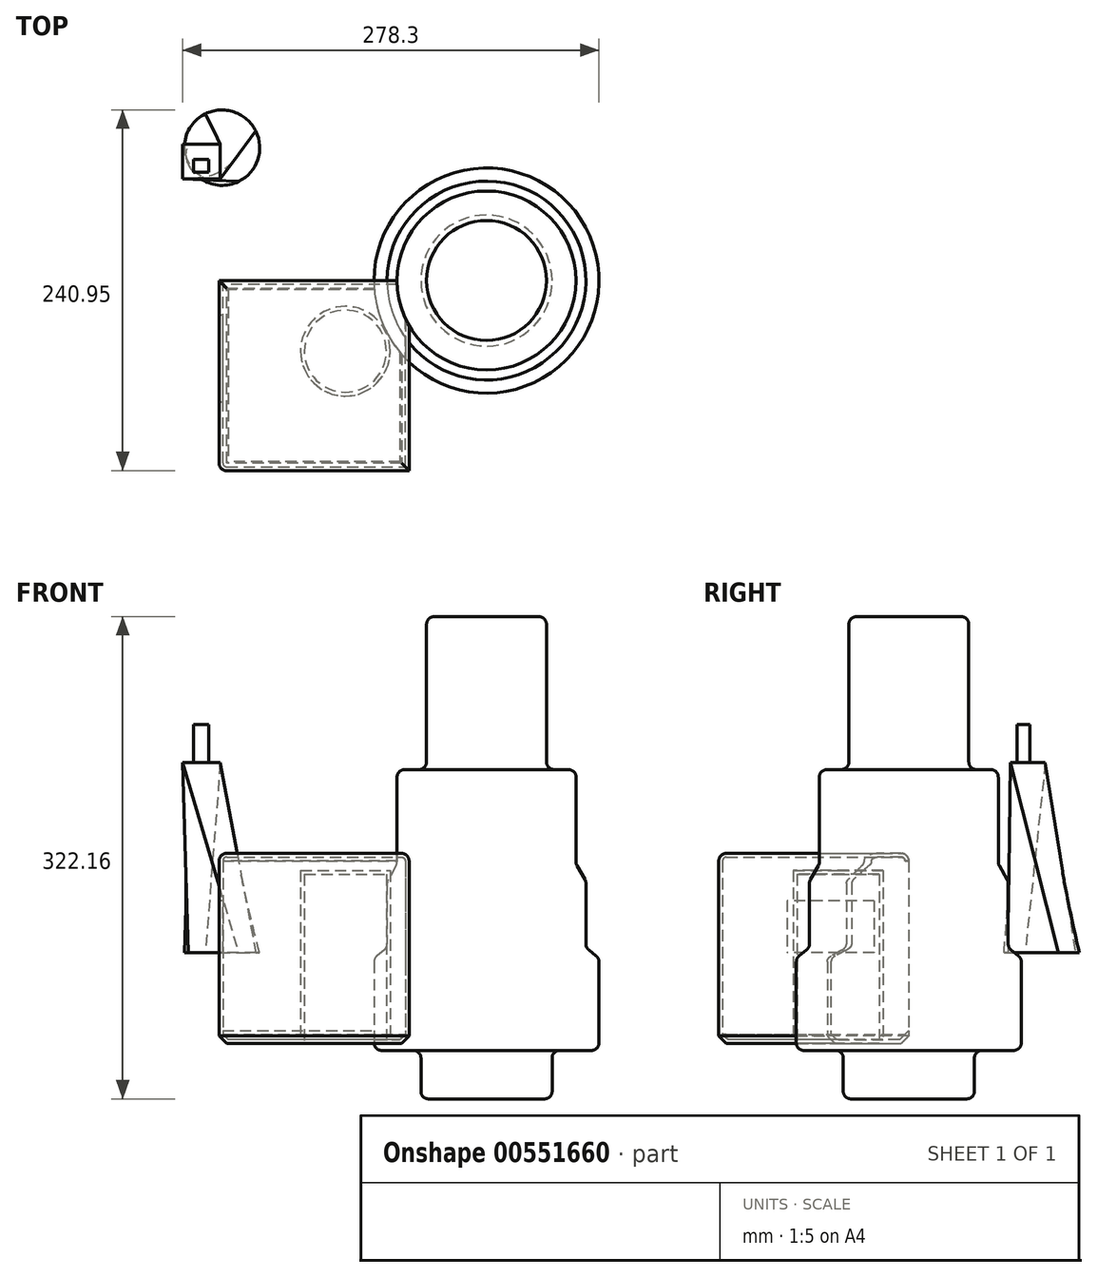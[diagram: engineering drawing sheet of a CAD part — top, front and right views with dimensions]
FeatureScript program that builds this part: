
annotation { "Feature Type Name" : "Feature", "Feature Type Description" : "" }
export const myFeature = defineFeature(function(context is Context, id is Id, definition is map)
    precondition{}
    {
        {
            var Q0;
            Q0=qCreatedBy(makeId("Front.planeOp"),FACE);
            var sketch = newSketch(context, id + "F0", { "sketchPlane" : qUnion([Q0])});
            skLineSegment(sketch, "E0.bottom", {"start": v(-66.33, 66.48) * mm, "end": v(60.67, 66.48) * mm});
            skLineSegment(sketch, "E0.top", {"start": v(-66.33, -60.52) * mm, "end": v(60.67, -60.52) * mm});
            skLineSegment(sketch, "E0.left", {"start": v(-66.33, 66.48) * mm, "end": v(-66.33, -60.52) * mm});
            skLineSegment(sketch, "E0.right", {"start": v(60.67, 66.48) * mm, "end": v(60.67, -60.52) * mm});
            skSolve(sketch);
        }
        {
            var Q0;
            Q0=makeQuery(id+"F0.imprint","IMPRINT",FACE,{"disambiguationData":[TD([[makeQuery(id+"F0.imprint","IMPRINT",EDGE,{"derivedFrom":sQuery(id+"F0.wireOp",EDGE,"E0.bottom")}),-1.0]])]});
            extrude(context, id + "F1", {"entities" : qUnion([Q0]), "depth" : 127 * mm, "offsetDistance" : 25.4 * mm});
        }
        {
            var Q0;
            Q0=makeQuery(id+"F1.opExtrude","SWEPT_FACE",FACE,{"disambiguationData":[OSD([sQuery(id+"F0.wireOp",EDGE,"E0.top")])]});
            var sketch = newSketch(context, id + "F2", { "sketchPlane" : qUnion([Q0])});
            skCircle(sketch, "E1", {"center": v(18.1, 47.2) * mm, "radius": 27.41 * mm});
            skSolve(sketch);
        }
        {
            var Q0;
            Q0=makeQuery(id+"F2.imprint","IMPRINT",FACE,{"disambiguationData":[TD([[makeQuery(id+"F2.imprint","IMPRINT",EDGE,{"derivedFrom":sQuery(id+"F2.wireOp",EDGE,"E1")}),1.0]])]});
            extrude(context, id + "F3", {"entities" : qUnion([Q0]), "operationType" : NewBodyOperationType.REMOVE, "oppositeDirection" : true, "depth" : 113.03 * mm, "offsetDistance" : 25.4 * mm});
        }
        {
            var Q0;
            Q0=qCreatedBy(makeId("Top.planeOp"),FACE);
            var sketch = newSketch(context, id + "F4", { "sketchPlane" : qUnion([Q0])});
            skCircle(sketch, "E2", {"center": v(-64.33, 88.76) * mm, "radius": 25.19 * mm});
            skSolve(sketch);
        }
        {
            var Q0;
            Q0=makeQuery(id+"F4.imprint","IMPRINT",FACE,{"disambiguationData":[TD([[makeQuery(id+"F4.imprint","IMPRINT",EDGE,{"derivedFrom":sQuery(id+"F4.wireOp",EDGE,"E2")}),1.0]])]});
            cPlane(context, id + "F5", {"entities" : qUnion([Q0]), "cplaneType" : CPlaneType.OFFSET, "offset" : 127 * mm, "width" : 152.4 * mm, "height" : 152.4 * mm});
        }
        {
            var Q0;
            Q0=qCreatedBy(id+"F5.planeOp",FACE);
            var sketch = newSketch(context, id + "F6", { "sketchPlane" : qUnion([Q0])});
            skLineSegment(sketch, "E3.bottom", {"start": v(-65.51, 91.17) * mm, "end": v(-90.73, 91.17) * mm});
            skLineSegment(sketch, "E3.top", {"start": v(-65.51, 67.95) * mm, "end": v(-90.73, 67.95) * mm});
            skLineSegment(sketch, "E3.left", {"start": v(-65.51, 91.17) * mm, "end": v(-65.51, 67.95) * mm});
            skLineSegment(sketch, "E3.right", {"start": v(-90.73, 91.17) * mm, "end": v(-90.73, 67.95) * mm});
            skSolve(sketch);
        }
        {
            var Q0;
            Q0=makeQuery(id+"F6.imprint","IMPRINT",FACE,{"disambiguationData":[TD([[makeQuery(id+"F6.imprint","IMPRINT",EDGE,{"derivedFrom":sQuery(id+"F6.wireOp",EDGE,"E3.bottom")}),1.0]])]});
            var Q1;
            Q1=makeQuery(id+"F4.imprint","IMPRINT",FACE,{"disambiguationData":[TD([[makeQuery(id+"F4.imprint","IMPRINT",EDGE,{"derivedFrom":sQuery(id+"F4.wireOp",EDGE,"E2")}),1.0]])]});
            loft(context, id + "F7", {"sheetProfilesArray" : [{ "sheetProfileEntities" : qUnion([Q0]) }, { "sheetProfileEntities" : qUnion([Q1]) }]});
        }
        {
            var Q0;
            Q0=makeQuery(id+"F1.opExtrude","CAP_EDGE",EDGE,{"disambiguationData":[OSD([sQuery(id+"F0.wireOp",EDGE,"E0.bottom")])],"isStart":false});
            var Q1;
            Q1=makeQuery(id+"F1.opExtrude","SWEPT_EDGE",EDGE,{"disambiguationData":[OSD([sQuery(id+"F0.wireOp",EDGE,"E0.bottom"),sQuery(id+"F0.wireOp",EDGE,"E0.right")])]});
            fillet(context, id + "F8", {"entities" : qUnion([Q0, Q1]), "radius" : 5.08 * mm, "tangentPropagation" : true, "allowEdgeOverflow" : false});
        }
        {
            var Q0;
            Q0=makeQuery(id+"F1.opExtrude","SWEPT_EDGE",EDGE,{"disambiguationData":[OSD([sQuery(id+"F0.wireOp",EDGE,"E0.bottom"),sQuery(id+"F0.wireOp",EDGE,"E0.left")])]});
            var Q1;
            Q1=makeQuery(id+"F1.opExtrude","CAP_EDGE",EDGE,{"disambiguationData":[OSD([sQuery(id+"F0.wireOp",EDGE,"E0.bottom")])],"isStart":true});
            fillet(context, id + "F9", {"entities" : qUnion([Q0, Q1]), "radius" : 5.08 * mm, "tangentPropagation" : true, "allowEdgeOverflow" : false});
        }
        {
            var Q0;
            Q0=makeQuery(id+"F1.opExtrude","CAP_EDGE",EDGE,{"disambiguationData":[OSD([sQuery(id+"F0.wireOp",EDGE,"E0.top")])],"isStart":false});
            var Q1;
            Q1=makeQuery(id+"F1.opExtrude","SWEPT_EDGE",EDGE,{"disambiguationData":[OSD([sQuery(id+"F0.wireOp",EDGE,"E0.top"),sQuery(id+"F0.wireOp",EDGE,"E0.right")])]});
            chamfer(context, id + "F10", {"entities" : qUnion([Q0, Q1]), "width" : 5.08 * mm, "tangentPropagation" : true});
        }
        {
            var Q0;
            Q0=makeQuery(id+"F1.opExtrude","CAP_FACE",FACE,{"disambiguationData":[OSD([sQuery(id+"F0.wireOp",EDGE,"E0.bottom"),sQuery(id+"F0.wireOp",EDGE,"E0.top"),sQuery(id+"F0.wireOp",EDGE,"E0.left"),sQuery(id+"F0.wireOp",EDGE,"E0.right")])],"isStart":true});
            shell(context, id + "F11", {"entities" : qUnion([Q0]), "thickness" : 2.54 * mm});
        }
        {
            var Q0;
            Q0=qCreatedBy(makeId("Front.planeOp"),FACE);
            var sketch = newSketch(context, id + "F12", { "sketchPlane" : qUnion([Q0])});
            skLineSegment(sketch, "E4", {"start": v(156.22, -97.54) * mm, "end": v(156.22, -65.19) * mm});
            skLineSegment(sketch, "E5", {"start": v(156.22, -65.19) * mm, "end": v(187.57, -65.19) * mm});
            skLineSegment(sketch, "E6", {"start": v(187.57, -65.19) * mm, "end": v(187.57, -3.63) * mm});
            skLineSegment(sketch, "E7", {"start": v(187.57, -3.63) * mm, "end": v(178.8, 3.54) * mm});
            skLineSegment(sketch, "E8", {"start": v(178.8, 3.54) * mm, "end": v(178.8, 47.71) * mm});
            skLineSegment(sketch, "E9", {"start": v(178.8, 47.71) * mm, "end": v(172.19, 59.38) * mm});
            skLineSegment(sketch, "E10", {"start": v(172.19, 59.38) * mm, "end": v(172.19, 122.45) * mm});
            skLineSegment(sketch, "E11", {"start": v(172.19, 122.45) * mm, "end": v(152.46, 122.45) * mm});
            skLineSegment(sketch, "E12", {"start": v(152.46, 122.45) * mm, "end": v(152.46, 224.62) * mm});
            skLineSegment(sketch, "E13", {"start": v(152.46, 224.62) * mm, "end": v(112.4, 224.62) * mm});
            skLineSegment(sketch, "E14", {"start": v(112.4, -97.54) * mm, "end": v(156.22, -97.54) * mm});
            skLineSegment(sketch, "E15", {"start": v(112.4, -97.54) * mm, "end": v(112.4, 288.31) * mm, "construction": true});
            skLineSegment(sketch, "E16", {"start": v(112.4, -97.54) * mm, "end": v(112.4, 224.62) * mm});
            skSolve(sketch);
        }
        {
            var Q0;
            Q0 = qSketchRegion(id + "F12", true);
            var Q1;
            Q1=sQuery(id+"F12.wireOp",EDGE,"E15");
            revolve(context, id + "F13", {"operationType" : NewBodyOperationType.ADD, "entities" : qUnion([Q0]), "axis" : qUnion([Q1]), "revolveType" : RevolveType.FULL});
        }
        {
            var Q0;
            Q0=makeQuery(id+"F13.opRevolve","SWEPT_EDGE",EDGE,{"disambiguationData":[OSD([sQuery(id+"F12.wireOp",EDGE,"E12"),sQuery(id+"F12.wireOp",EDGE,"E13")])]});
            var Q1;
            Q1=makeQuery(id+"F13.opRevolve","SWEPT_EDGE",EDGE,{"disambiguationData":[OSD([sQuery(id+"F12.wireOp",EDGE,"E11"),sQuery(id+"F12.wireOp",EDGE,"E12")])]});
            var Q2;
            Q2=makeQuery(id+"F13.opRevolve","SWEPT_EDGE",EDGE,{"disambiguationData":[OSD([sQuery(id+"F12.wireOp",EDGE,"E10"),sQuery(id+"F12.wireOp",EDGE,"E11")])]});
            var Q3;
            Q3=makeQuery(id+"F13.opRevolve","SWEPT_EDGE",EDGE,{"disambiguationData":[OSD([sQuery(id+"F12.wireOp",EDGE,"E9"),sQuery(id+"F12.wireOp",EDGE,"E10")])]});
            var Q4;
            Q4=makeQuery(id+"F13.opRevolve","SWEPT_EDGE",EDGE,{"disambiguationData":[OSD([sQuery(id+"F12.wireOp",EDGE,"E8"),sQuery(id+"F12.wireOp",EDGE,"E9")])]});
            var Q5;
            Q5=makeQuery(id+"F13.opRevolve","SWEPT_EDGE",EDGE,{"disambiguationData":[OSD([sQuery(id+"F12.wireOp",EDGE,"E7"),sQuery(id+"F12.wireOp",EDGE,"E8")])]});
            var Q6;
            Q6=makeQuery(id+"F13.opRevolve","SWEPT_EDGE",EDGE,{"disambiguationData":[OSD([sQuery(id+"F12.wireOp",EDGE,"E6"),sQuery(id+"F12.wireOp",EDGE,"E7")])]});
            var Q7;
            Q7=makeQuery(id+"F13.opRevolve","SWEPT_EDGE",EDGE,{"disambiguationData":[OSD([sQuery(id+"F12.wireOp",EDGE,"E5"),sQuery(id+"F12.wireOp",EDGE,"E6")])]});
            var Q8;
            Q8=makeQuery(id+"F13.opRevolve","SWEPT_EDGE",EDGE,{"disambiguationData":[OSD([sQuery(id+"F12.wireOp",EDGE,"E4"),sQuery(id+"F12.wireOp",EDGE,"E5")])]});
            var Q9;
            Q9=makeQuery(id+"F13.opRevolve","SWEPT_EDGE",EDGE,{"disambiguationData":[OSD([sQuery(id+"F12.wireOp",EDGE,"E4"),sQuery(id+"F12.wireOp",EDGE,"E14")])]});
            fillet(context, id + "F14", {"entities" : qUnion([Q0, Q1, Q2, Q3, Q4, Q5, Q6, Q7, Q8, Q9]), "radius" : 5.08 * mm, "tangentPropagation" : true, "allowEdgeOverflow" : false});
        }
        {
            var Q0;
            Q0=makeQuery(id+"F7.opLoft","CAP_FACE",FACE,{"disambiguationData":[OSD([makeQuery(id+"F6.imprint","IMPRINT",FACE,{"disambiguationData":[TD([[makeQuery(id+"F6.imprint","IMPRINT",EDGE,{"derivedFrom":sQuery(id+"F6.wireOp",EDGE,"E3.bottom")}),1.0]])]})])],"isStart":true});
            var sketch = newSketch(context, id + "F15", { "sketchPlane" : qUnion([Q0])});
            skLineSegment(sketch, "E17.bottom", {"start": v(-73.08, 80.76) * mm, "end": v(-83.23, 80.76) * mm});
            skLineSegment(sketch, "E17.top", {"start": v(-73.08, 72.3) * mm, "end": v(-83.23, 72.3) * mm});
            skLineSegment(sketch, "E17.left", {"start": v(-73.08, 80.76) * mm, "end": v(-73.08, 72.3) * mm});
            skLineSegment(sketch, "E17.right", {"start": v(-83.23, 80.76) * mm, "end": v(-83.23, 72.3) * mm});
            skSolve(sketch);
        }
        {
            var Q0;
            Q0 = qSketchRegion(id + "F15", true);
            extrude(context, id + "F16", {"entities" : qUnion([Q0]), "operationType" : NewBodyOperationType.ADD, "depth" : 25.4 * mm, "offsetDistance" : 25.4 * mm});
        }
        {
            var Q0;
            Q0=makeQuery(id+"F1.opExtrude","SWEPT_FACE",FACE,{"disambiguationData":[OSD([sQuery(id+"F0.wireOp",EDGE,"E0.left")])]});
            var sketch = newSketch(context, id + "F17", { "sketchPlane" : qUnion([Q0])});
            skLineSegment(sketch, "E18.bottom", {"start": v(23.15, 34.84) * mm, "end": v(81.4, 34.84) * mm});
            skLineSegment(sketch, "E18.top", {"start": v(23.15, 0) * mm, "end": v(81.4, 0) * mm});
            skLineSegment(sketch, "E18.left", {"start": v(23.15, 34.84) * mm, "end": v(23.15, 0) * mm});
            skLineSegment(sketch, "E18.right", {"start": v(81.4, 34.84) * mm, "end": v(81.4, 0) * mm});
            skSolve(sketch);
        }
        {
            var Q0;
            Q0 = qSketchRegion(id + "F17", true);
            extrude(context, id + "F18", {"entities" : qUnion([Q0]), "operationType" : NewBodyOperationType.REMOVE, "oppositeDirection" : true, "depth" : 25.4 * mm, "offsetDistance" : 25.4 * mm});
        }
    });
